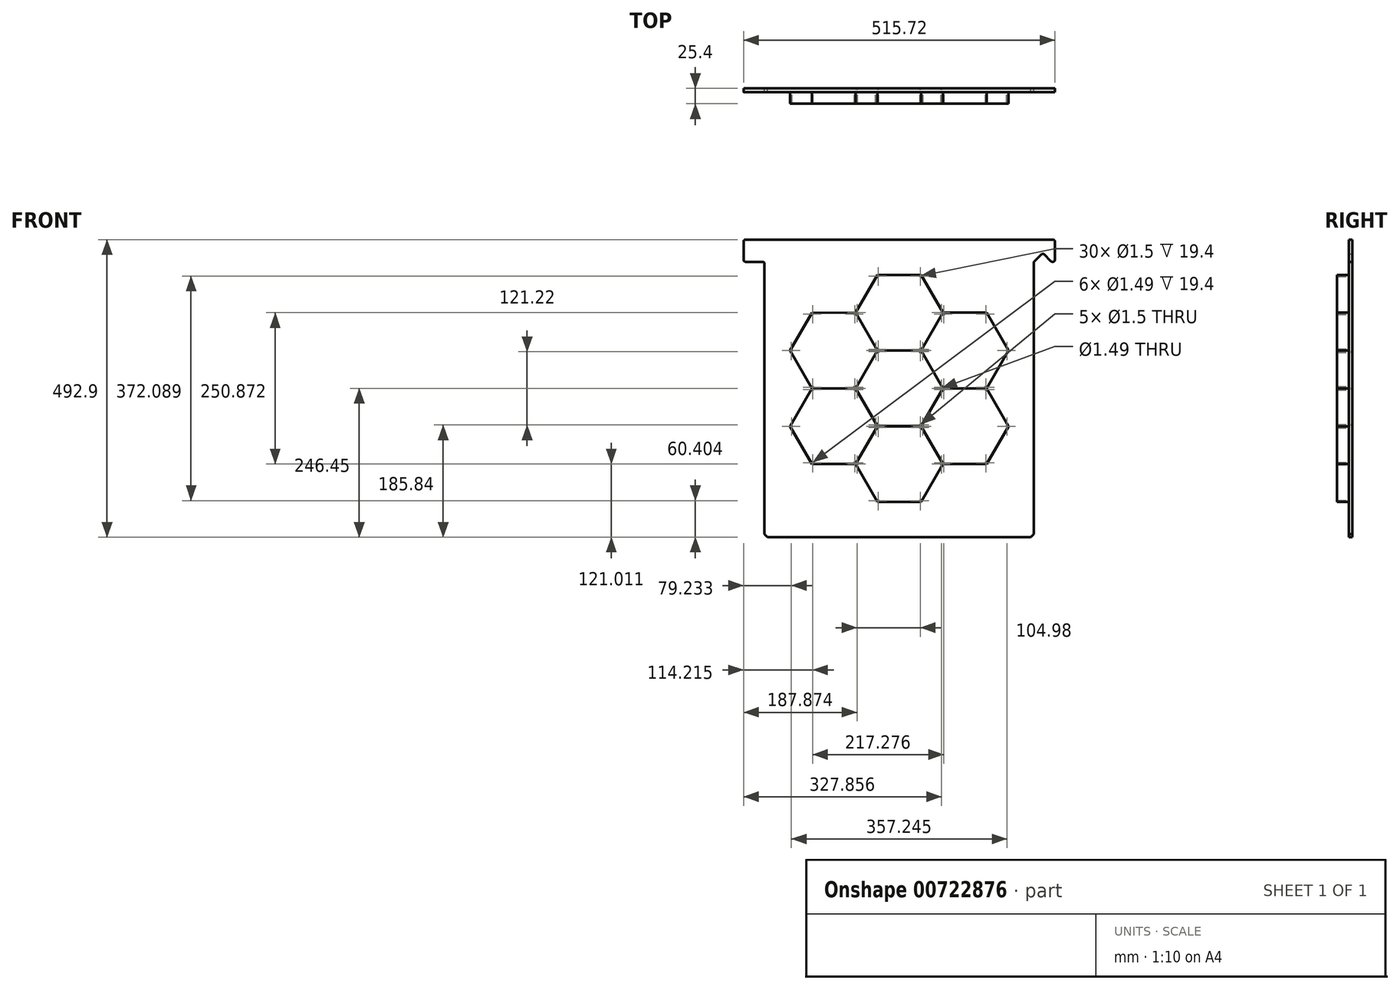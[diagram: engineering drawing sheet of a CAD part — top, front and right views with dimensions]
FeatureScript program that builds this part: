
annotation { "Feature Type Name" : "Feature", "Feature Type Description" : "" }
export const myFeature = defineFeature(function(context is Context, id is Id, definition is map)
    precondition{}
    {
        {
            var Q0;
            Q0=qCreatedBy(makeId("Front.planeOp"),FACE);
            var sketch = newSketch(context, id + "F0", { "sketchPlane" : qUnion([Q0])});
            skLineSegment(sketch, "E0", {"start": v(72.3, 0) * mm, "end": v(36.15, 62.61) * mm});
            skLineSegment(sketch, "E1", {"start": v(36.15, 62.61) * mm, "end": v(-36.15, 62.61) * mm});
            skLineSegment(sketch, "E2", {"start": v(-36.15, 62.61) * mm, "end": v(-72.3, 0) * mm});
            skLineSegment(sketch, "E3", {"start": v(-72.3, 0) * mm, "end": v(-36.15, -62.61) * mm});
            skLineSegment(sketch, "E4", {"start": v(-36.15, -62.61) * mm, "end": v(36.15, -62.61) * mm});
            skLineSegment(sketch, "E5", {"start": v(36.15, -62.61) * mm, "end": v(72.3, 0) * mm});
            skCircle(sketch, "E6", {"center": v(35, 60.6) * mm, "radius": 0.75 * mm});
            skCircle(sketch, "E7", {"center": v(-35, 60.6) * mm, "radius": 0.75 * mm});
            skCircle(sketch, "E8", {"center": v(35, -60.6) * mm, "radius": 0.75 * mm});
            skCircle(sketch, "E9", {"center": v(-35, -60.6) * mm, "radius": 0.75 * mm});
            skCircle(sketch, "E10", {"center": v(-69.99, 0) * mm, "radius": 0.75 * mm});
            skPoint(sketch, "E11", {"position": v(70, 0) * mm});
            skCircle(sketch, "E12", {"center": v(70, 0) * mm, "radius": 0.74 * mm});
            skLineSegment(sketch, "E13.MirrorCS", {"start": v(36.34, -62.72) * mm, "end": v(72.48, -0.1) * mm});
            skCircle(sketch, "E14.MirrorC", {"center": v(38.65, -62.72) * mm, "radius": 0.75 * mm});
            skLineSegment(sketch, "E15.MirrorCS", {"start": v(72.49, -125.33) * mm, "end": v(36.34, -62.72) * mm});
            skLineSegment(sketch, "E16.MirrorCS", {"start": v(72.48, -0.1) * mm, "end": v(144.78, -0.1) * mm});
            skCircle(sketch, "E17.MirrorC", {"center": v(73.63, -2.1) * mm, "radius": 0.74 * mm});
            skCircle(sketch, "E18.MirrorC", {"center": v(143.62, -2.1) * mm, "radius": 0.75 * mm});
            skLineSegment(sketch, "E19.MirrorCS", {"start": v(144.78, -0.1) * mm, "end": v(180.93, -62.7) * mm});
            skLineSegment(sketch, "E20.MirrorCS", {"start": v(180.93, -62.7) * mm, "end": v(144.78, -125.32) * mm});
            skCircle(sketch, "E21.MirrorC", {"center": v(178.62, -62.7) * mm, "radius": 0.75 * mm});
            skLineSegment(sketch, "E22.MirrorCS", {"start": v(144.78, -125.32) * mm, "end": v(72.49, -125.33) * mm});
            skCircle(sketch, "E23.MirrorC", {"center": v(73.64, -123.33) * mm, "radius": 0.75 * mm});
            skCircle(sketch, "E24.MirrorC", {"center": v(143.63, -123.32) * mm, "radius": 0.75 * mm});
            skLineSegment(sketch, "E25.MirrorCS", {"start": v(-36.15, -62.82) * mm, "end": v(36.15, -62.83) * mm});
            skLineSegment(sketch, "E26.MirrorCS", {"start": v(-72.3, -125.43) * mm, "end": v(-36.15, -62.82) * mm});
            skCircle(sketch, "E27.MirrorC", {"center": v(-35, -64.82) * mm, "radius": 0.75 * mm});
            skCircle(sketch, "E28.MirrorC", {"center": v(35, -64.83) * mm, "radius": 0.75 * mm});
            skLineSegment(sketch, "E29.MirrorCS", {"start": v(72.3, -125.44) * mm, "end": v(36.14, -188.05) * mm});
            skLineSegment(sketch, "E30.MirrorCS", {"start": v(36.14, -188.05) * mm, "end": v(-36.16, -188.04) * mm});
            skLineSegment(sketch, "E31.MirrorCS", {"start": v(-36.16, -188.04) * mm, "end": v(-72.3, -125.43) * mm});
            skLineSegment(sketch, "E32.MirrorCS", {"start": v(36.15, -62.83) * mm, "end": v(72.3, -125.44) * mm});
            skCircle(sketch, "E33.MirrorC", {"center": v(70, -125.44) * mm, "radius": 0.74 * mm});
            skCircle(sketch, "E34.MirrorC", {"center": v(34.98, -186.05) * mm, "radius": 0.75 * mm});
            skCircle(sketch, "E35.MirrorC", {"center": v(-35, -186.04) * mm, "radius": 0.75 * mm});
            skCircle(sketch, "E36.MirrorC", {"center": v(-70, -125.43) * mm, "radius": 0.75 * mm});
            skLineSegment(sketch, "E37.MirrorCS", {"start": v(-72.46, -0.1) * mm, "end": v(-36.32, -62.7) * mm});
            skLineSegment(sketch, "E38.MirrorCS", {"start": v(-144.75, -0.08) * mm, "end": v(-72.46, -0.1) * mm});
            skCircle(sketch, "E39.MirrorC", {"center": v(-73.61, -2.1) * mm, "radius": 0.75 * mm});
            skCircle(sketch, "E40.MirrorC", {"center": v(-38.63, -62.7) * mm, "radius": 0.75 * mm});
            skLineSegment(sketch, "E41.MirrorCS", {"start": v(-36.32, -62.7) * mm, "end": v(-72.48, -125.31) * mm});
            skCircle(sketch, "E42.MirrorC", {"center": v(-73.63, -123.31) * mm, "radius": 0.75 * mm});
            skLineSegment(sketch, "E43.MirrorCS", {"start": v(-72.48, -125.31) * mm, "end": v(-144.77, -125.3) * mm});
            skCircle(sketch, "E44.MirrorC", {"center": v(-143.62, -123.31) * mm, "radius": 0.74 * mm});
            skLineSegment(sketch, "E45.MirrorCS", {"start": v(-144.77, -125.3) * mm, "end": v(-180.91, -62.69) * mm});
            skLineSegment(sketch, "E46.MirrorCS", {"start": v(-180.91, -62.69) * mm, "end": v(-144.75, -0.08) * mm});
            skCircle(sketch, "E47.MirrorC", {"center": v(-143.6, -2.08) * mm, "radius": 0.75 * mm});
            skCircle(sketch, "E48.MirrorC", {"center": v(-178.6, -62.69) * mm, "radius": 0.75 * mm});
            skLineSegment(sketch, "E49.MirrorCS", {"start": v(-36.34, 62.72) * mm, "end": v(-72.49, 0.1) * mm});
            skLineSegment(sketch, "E50.MirrorCS", {"start": v(-72.5, 125.33) * mm, "end": v(-36.34, 62.72) * mm});
            skCircle(sketch, "E51.MirrorC", {"center": v(-38.65, 62.72) * mm, "radius": 0.75 * mm});
            skCircle(sketch, "E52.MirrorC", {"center": v(-73.65, 123.33) * mm, "radius": 0.75 * mm});
            skLineSegment(sketch, "E53.MirrorCS", {"start": v(-144.8, 125.32) * mm, "end": v(-72.5, 125.33) * mm});
            skCircle(sketch, "E54.MirrorC", {"center": v(-143.65, 123.33) * mm, "radius": 0.74 * mm});
            skLineSegment(sketch, "E55.MirrorCS", {"start": v(-180.94, 62.7) * mm, "end": v(-144.8, 125.32) * mm});
            skLineSegment(sketch, "E56.MirrorCS", {"start": v(-144.78, 0.1) * mm, "end": v(-180.94, 62.7) * mm});
            skCircle(sketch, "E57.MirrorC", {"center": v(-178.63, 62.7) * mm, "radius": 0.75 * mm});
            skCircle(sketch, "E58.MirrorC", {"center": v(-143.63, 2.1) * mm, "radius": 0.75 * mm});
            skLineSegment(sketch, "E59.MirrorCS", {"start": v(-72.49, 0.1) * mm, "end": v(-144.78, 0.1) * mm});
            skCircle(sketch, "E60.MirrorC", {"center": v(-73.64, 2.1) * mm, "radius": 0.75 * mm});
            skLineSegment(sketch, "E61.MirrorCS", {"start": v(36.15, 62.82) * mm, "end": v(-36.15, 62.82) * mm});
            skLineSegment(sketch, "E62.MirrorCS", {"start": v(-36.15, 62.82) * mm, "end": v(-72.3, 125.43) * mm});
            skCircle(sketch, "E63.MirrorC", {"center": v(-35, 64.82) * mm, "radius": 0.75 * mm});
            skCircle(sketch, "E64.MirrorC", {"center": v(35, 64.82) * mm, "radius": 0.75 * mm});
            skLineSegment(sketch, "E65.MirrorCS", {"start": v(72.3, 125.43) * mm, "end": v(36.15, 62.82) * mm});
            skCircle(sketch, "E66.MirrorC", {"center": v(70, 125.43) * mm, "radius": 0.74 * mm});
            skLineSegment(sketch, "E67.MirrorCS", {"start": v(36.15, 188.04) * mm, "end": v(72.3, 125.43) * mm});
            skLineSegment(sketch, "E68.MirrorCS", {"start": v(-36.15, 188.04) * mm, "end": v(36.15, 188.04) * mm});
            skCircle(sketch, "E69.MirrorC", {"center": v(35, 186.04) * mm, "radius": 0.75 * mm});
            skLineSegment(sketch, "E70.MirrorCS", {"start": v(-72.3, 125.43) * mm, "end": v(-36.15, 188.04) * mm});
            skCircle(sketch, "E71.MirrorC", {"center": v(-35, 186.04) * mm, "radius": 0.75 * mm});
            skCircle(sketch, "E72.MirrorC", {"center": v(-69.99, 125.43) * mm, "radius": 0.75 * mm});
            skLineSegment(sketch, "E73.MirrorCS", {"start": v(72.48, 0.1) * mm, "end": v(36.32, 62.71) * mm});
            skLineSegment(sketch, "E74.MirrorCS", {"start": v(36.32, 62.71) * mm, "end": v(72.46, 125.33) * mm});
            skCircle(sketch, "E75.MirrorC", {"center": v(38.63, 62.71) * mm, "radius": 0.75 * mm});
            skCircle(sketch, "E76.MirrorC", {"center": v(73.62, 123.33) * mm, "radius": 0.75 * mm});
            skLineSegment(sketch, "E77.MirrorCS", {"start": v(72.46, 125.33) * mm, "end": v(144.76, 125.34) * mm});
            skLineSegment(sketch, "E78.MirrorCS", {"start": v(144.76, 125.34) * mm, "end": v(180.92, 62.73) * mm});
            skCircle(sketch, "E79.MirrorC", {"center": v(143.6, 123.34) * mm, "radius": 0.75 * mm});
            skLineSegment(sketch, "E80.MirrorCS", {"start": v(180.92, 62.73) * mm, "end": v(144.78, 0.12) * mm});
            skCircle(sketch, "E81.MirrorC", {"center": v(178.6, 62.73) * mm, "radius": 0.75 * mm});
            skLineSegment(sketch, "E82.MirrorCS", {"start": v(144.78, 0.12) * mm, "end": v(72.48, 0.1) * mm});
            skCircle(sketch, "E83.MirrorC", {"center": v(143.62, 2.12) * mm, "radius": 0.75 * mm});
            skCircle(sketch, "E84.MirrorC", {"center": v(73.63, 2.1) * mm, "radius": 0.74 * mm});
            skSolve(sketch);
        }
        {
            var Q0;
            Q0=makeQuery(id+"F0.imprint","IMPRINT",FACE,{"disambiguationData":[TD([[makeQuery(id+"F0.imprint","IMPRINT",EDGE,{"derivedFrom":sQuery(id+"F0.wireOp",EDGE,"E0")}),1.0]])]});
            var sketch = newSketch(context, id + "F1", { "sketchPlane" : qUnion([Q0])});
            skLineSegment(sketch, "E85", {"start": v(251.18, 210.64) * mm, "end": v(239.93, 222.08) * mm});
            skArc(sketch, "E86", {"start": v(251.18, 210.64) * mm, "mid": v(252.15, 209.99) * mm, "end": v(253.3, 209.76) * mm});
            skLineSegment(sketch, "E87", {"start": v(254.88, 209.76) * mm, "end": v(253.3, 209.76) * mm});
            skArc(sketch, "E88", {"start": v(254.88, 209.76) * mm, "mid": v(256.98, 210.63) * mm, "end": v(257.86, 212.73) * mm});
            skLineSegment(sketch, "E89", {"start": v(257.86, 243.48) * mm, "end": v(257.86, 212.73) * mm});
            skArc(sketch, "E90", {"start": v(257.86, 243.48) * mm, "mid": v(256.98, 245.58) * mm, "end": v(254.88, 246.45) * mm});
            skLineSegment(sketch, "E91", {"start": v(-254.88, 246.45) * mm, "end": v(254.88, 246.45) * mm});
            skArc(sketch, "E92", {"start": v(-254.88, 246.45) * mm, "mid": v(-256.98, 245.58) * mm, "end": v(-257.86, 243.48) * mm});
            skLineSegment(sketch, "E93", {"start": v(-257.86, 212.73) * mm, "end": v(-257.86, 243.48) * mm});
            skArc(sketch, "E94", {"start": v(-257.86, 212.73) * mm, "mid": v(-256.98, 210.63) * mm, "end": v(-254.88, 209.76) * mm});
            skLineSegment(sketch, "E95", {"start": v(-226.12, 209.76) * mm, "end": v(-254.88, 209.76) * mm});
            skArc(sketch, "E96", {"start": v(-226.12, 209.76) * mm, "mid": v(-224.02, 208.88) * mm, "end": v(-223.14, 206.78) * mm});
            skLineSegment(sketch, "E97", {"start": v(-223.14, -241.5) * mm, "end": v(-223.14, 206.78) * mm});
            skLineSegment(sketch, "E98", {"start": v(-223.14, -241.5) * mm, "end": v(-218.19, -246.45) * mm});
            skLineSegment(sketch, "E99", {"start": v(218.19, -246.45) * mm, "end": v(-218.19, -246.45) * mm});
            skLineSegment(sketch, "E100", {"start": v(218.19, -246.45) * mm, "end": v(223.14, -241.5) * mm});
            skLineSegment(sketch, "E101", {"start": v(223.14, 208.5) * mm, "end": v(223.14, -241.5) * mm});
            skArc(sketch, "E102", {"start": v(223.14, 208.5) * mm, "mid": v(223.38, 209.66) * mm, "end": v(224.03, 210.63) * mm});
            skLineSegment(sketch, "E103", {"start": v(235.72, 222.12) * mm, "end": v(224.03, 210.63) * mm});
            skArc(sketch, "E104", {"start": v(235.72, 222.12) * mm, "mid": v(237.83, 222.97) * mm, "end": v(239.93, 222.08) * mm});
            skSolve(sketch);
        }
        {
            var Q0;
            Q0=makeQuery(id+"F1.imprint","IMPRINT",FACE,{"disambiguationData":[TD([[makeQuery(id+"F1.imprint","IMPRINT",EDGE,{"derivedFrom":sQuery(id+"F1.wireOp",EDGE,"E85")}),-1.0]])]});
            extrude(context, id + "F2", {"entities" : qUnion([Q0]), "depth" : 6 * mm, "offsetDistance" : 25.4 * mm});
        }
        {
            var Q0;
            Q0 = qSketchRegion(id + "F0", true);
            extrude(context, id + "F3", {"entities" : qUnion([Q0]), "operationType" : NewBodyOperationType.ADD, "depth" : 25.4 * mm, "offsetDistance" : 25.4 * mm});
        }
    });
